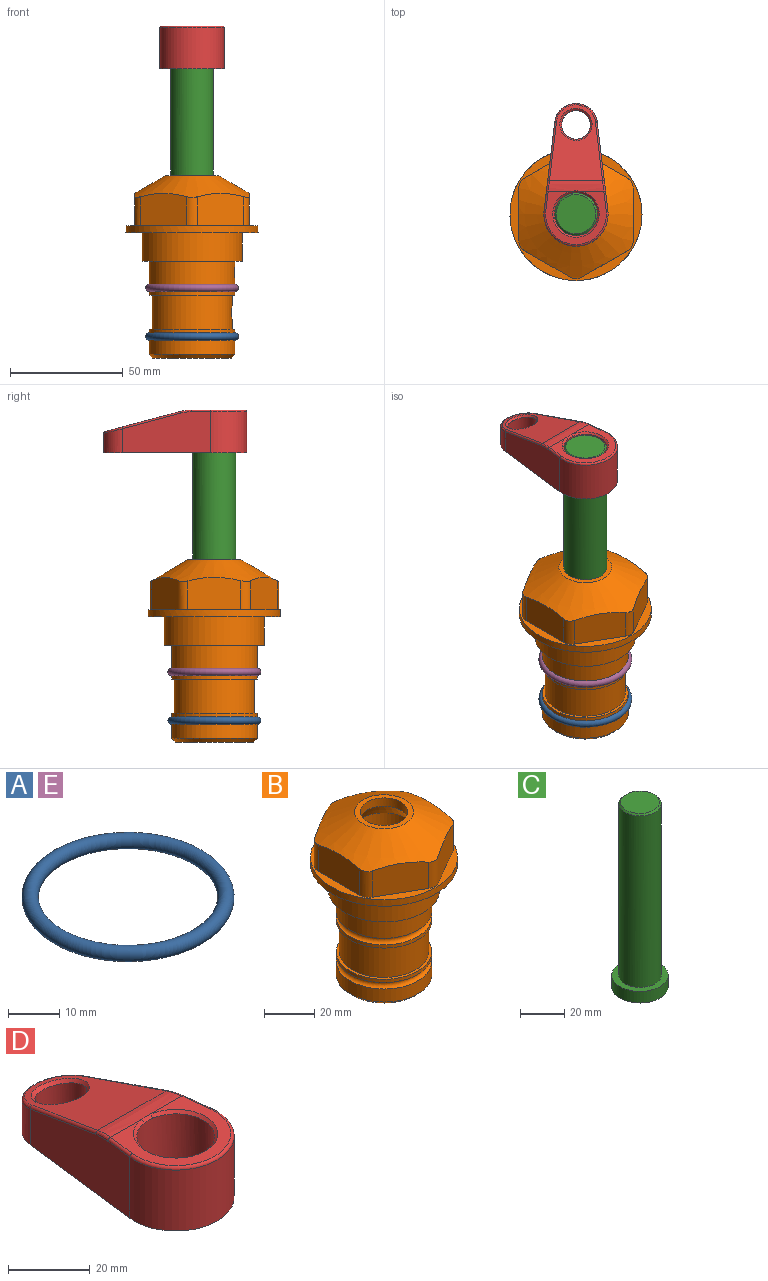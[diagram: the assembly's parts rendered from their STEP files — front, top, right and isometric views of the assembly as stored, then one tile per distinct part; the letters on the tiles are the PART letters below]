
ASSEMBLY  parts=5 mates=4
PART A: 1 faces, bbox 44.7x44.7x3.2 mm
  f0: torus R=19.05mm, axis (0,0,1), area 1193.9mm2
PART B: 36 faces, bbox 58.7x58.7x81 mm
  f0: cylinder r=17.78mm len=35.56mm, axis (0,0,1), area 1670.8mm2, adj f23,f24,f31
  f1: cylinder r=19.05mm len=38.1mm, axis (0,0,1), area 1191.9mm2, adj f26,f27,f30
  f2: plane 58.66x58.66mm, normal (0,0,-1), area 1150.6mm2, adj f3,f28
  f3: cylinder r=29.33mm len=58.66mm, axis (0,0,-1), area 585.1mm2, adj f2,f4
  f4: plane 58.66x58.66mm, normal (0,0,1), area 475.9mm2, adj f3,f5,f6,f7,f8,f9,f10,f11
  f5: plane 20.32x14.34mm, normal (-0.5,0.87,0), area 324.4mm2, adj f4,f15,f16,f17
  f6: plane 20.32x14.34mm, normal (0.5,0.87,0), area 324.4mm2, adj f4,f14,f15,f17
  f7: plane 23.48x14.34mm, normal (1,0,0), area 324.4mm2, adj f4,f13,f14,f17
  f8: plane 20.32x14.34mm, normal (0.5,-0.87,0), area 324.4mm2, adj f4,f12,f13,f17
  f9: plane 20.32x14.34mm, normal (-0.5,-0.87,0), area 324.4mm2, adj f4,f11,f12,f17
  f10: plane 23.48x14.34mm, normal (-1,0,0), area 324.4mm2, adj f4,f11,f16,f17
  f11: cylinder r=5.08mm len=12.85mm, axis (0,0,-1), area 67.2mm2, adj f4,f9,f10,f17
  f12: cylinder r=5.08mm len=12.85mm, axis (0,0,-1), area 67.2mm2, adj f4,f8,f9,f17
  f13: cylinder r=5.08mm len=12.85mm, axis (0,0,-1), area 67.2mm2, adj f4,f7,f8,f17
  f14: cylinder r=5.08mm len=12.85mm, axis (0,0,-1), area 67.2mm2, adj f4,f6,f7,f17
  f15: cylinder r=5.08mm len=12.85mm, axis (0,0,-1), area 67.2mm2, adj f4,f5,f6,f17
  f16: cylinder r=5.08mm len=12.85mm, axis (0,0,-1), area 67.2mm2, adj f4,f5,f10,f17
  f17: cone r=11.73mm half-angle=60deg, axis (0,0,-1), area 2071.8mm2, adj f5,f6,f7,f8,f9,f10,f11,f12
  f18: plane 23.46x23.46mm, normal (0,0,1), area 147.4mm2, adj f17,f35
  f19: plane 34.93x34.93mm, normal (0,0,-1), area 958mm2, adj f29
  f20: cylinder r=19.05mm len=38.1mm, axis (0,0,1), area 760.1mm2, adj f21,f29
  f21: torus R=19.05mm, axis (0,0,1), area 565.3mm2, adj f20,f22
  f22: cylinder r=19.05mm len=38.1mm, axis (0,0,1), area 190mm2, adj f21,f23
  f23: plane 38.1x38.1mm, normal (0,0,1), area 146.9mm2, adj f0,f22
  f24: plane 38.1x38.1mm, normal (0,0,-1), area 146.9mm2, adj f0,f25
  f25: cylinder r=19.05mm len=38.1mm, axis (0,0,1), area 190mm2, adj f24,f26
  f26: torus R=19.05mm, axis (0,0,1), area 565.3mm2, adj f1,f25
  f27: plane 44.45x44.45mm, normal (0,0,-1), area 411.7mm2, adj f1,f28
  f28: cylinder r=22.23mm len=44.45mm, axis (0,0,1), area 1773.5mm2, adj f2,f27
  f29: cone r=19.05mm half-angle=45deg, axis (0,0,1), area 257.5mm2, adj f19,f20
  f30: cylinder r=3.17mm len=6.75mm, axis (-1,0,0), area 128mm2, adj f1,f33
  f31: cylinder r=3.17mm len=6.35mm, axis (-1,0,0), area 102.5mm2, adj f0,f33
  f32: plane 25.4x25.4mm, normal (0,0,1), area 506.7mm2, adj f33
  f33: cylinder r=12.7mm len=66.42mm, axis (0,0,-1), area 5236.2mm2, adj f30,f31,f32,f34
  f34: cone r=9.53mm half-angle=30deg, axis (0,0,-1), area 443.4mm2, adj f33,f35
  f35: cylinder r=9.53mm len=19.05mm, axis (0,0,-1), area 240.9mm2, adj f18,f34
PART C: 6 faces, bbox 25.4x25.4x101.6 mm
  f0: plane 17.46x17.46mm, normal (0,0,1), area 239.5mm2, adj f5
  f1: plane 25.4x25.4mm, normal (0,0,-1), area 506.7mm2, adj f2
  f2: cylinder r=12.7mm len=25.4mm, axis (0,0,1), area 506.7mm2, adj f1,f3
  f3: plane 25.4x25.4mm, normal (0,0,1), area 221.7mm2, adj f2,f4
  f4: cylinder r=9.53mm len=94.46mm, axis (0,0,1), area 5653mm2, adj f3,f5
  f5: cone r=8.73mm half-angle=45deg, axis (0,0,-1), area 64.4mm2, adj f0,f4
PART D: 31 faces, bbox 31.7x65.5x19.8 mm
  f0: plane 39.12x18.26mm, normal (0.99,0.12,0), area 612.2mm2, adj f1,f4,f7,f11,f13,f15
  f1: cylinder r=9.53mm len=18.91mm, axis (0,0,-1), area 296.1mm2, adj f0,f2,f7,f17
  f2: plane 39.12x18.26mm, normal (-0.99,0.12,0), area 612.2mm2, adj f1,f4,f7,f12,f14,f16
  f3: cylinder r=6.35mm len=12.7mm, axis (0,0,-1), area 362.4mm2, adj f7,f18
  f4: cylinder r=14.29mm len=28.58mm, axis (0,0,-1), area 882.2mm2, adj f0,f2,f7,f10
  f5: cylinder r=9.53mm len=19.05mm, axis (0,0,-1), area 1092.6mm2, adj f7,f19,f20
  f6: plane 26.99x23.69mm, normal (0,0,1), area 216.2mm2, adj f9,f10,f11,f12,f19
  f7: plane 63.5x28.58mm, normal (0,0,-1), area 661.8mm2, adj f0,f1,f2,f3,f4,f5,f22,f23
  f8: plane 33.52x23.6mm, normal (0,0.26,0.97), area 486mm2, adj f9,f15,f16,f17,f18
  f9: cylinder r=19.05mm len=24.72mm, axis (1,0,0), area 120.4mm2, adj f6,f8,f13,f14,f20
  f10: torus R=13.49mm, axis (0,0,1), area 59mm2, adj f4,f6,f11,f12
  f11: cylinder r=0.79mm len=8.67mm, axis (0.12,-0.99,0), area 10.8mm2, adj f0,f6,f10,f13
  f12: cylinder r=0.79mm len=8.67mm, axis (0.12,0.99,0), area 10.8mm2, adj f2,f6,f10,f14
  f13: bspline ~4.95x1.42mm, area 6.1mm2, adj f0,f9,f11,f15
  f14: bspline ~4.95x1.42mm, area 6.1mm2, adj f2,f9,f12,f16
  f15: cylinder r=0.79mm len=25.95mm, axis (0.12,-0.96,0.26), area 32.9mm2, adj f0,f8,f13,f17
  f16: cylinder r=0.79mm len=25.95mm, axis (0.12,0.96,-0.26), area 32.9mm2, adj f2,f8,f14,f17
  f17: bspline ~18.91x8.38mm, area 30mm2, adj f1,f8,f15,f16
  f18: bspline ~14.29x14.29mm, area 48.3mm2, adj f3,f8
  f19: cone r=9.53mm half-angle=45deg, axis (0,0,1), area 66.5mm2, adj f5,f6,f20
  f20: bspline ~3.22x0.96mm, area 3.5mm2, adj f5,f9,f19
  f21: plane 2.75x2.72mm, normal (0,0,-1), area 2.9mm2, adj f23,f25,f28
  f22: plane 23.05x15.88mm, normal (-0.99,-0.12,0), area 323.6mm2, adj f7,f25,f26,f27,f28,f29
  f23: plane 23.05x15.88mm, normal (0.99,-0.12,0), area 323.6mm2, adj f7,f21,f25,f27,f28,f30
  f24: cylinder r=9.53mm len=10.69mm, axis (0,0,-1), area 114.7mm2, adj f7,f27,f29,f30
  f25: cylinder r=12.7mm len=20.59mm, axis (0,0,-1), area 381.1mm2, adj f7,f21,f22,f23,f26,f28
  f26: plane 2.75x2.72mm, normal (0,0,-1), area 2.9mm2, adj f22,f25,f28
  f27: plane 19.72x18.37mm, normal (0,-0.26,-0.97), area 291.8mm2, adj f22,f23,f24,f28,f29,f30
  f28: cylinder r=15.88mm len=19.92mm, axis (1,0,0), area 54.8mm2, adj f21,f22,f23,f25,f26,f27
  f29: cylinder r=1.59mm len=11mm, axis (0,0,-1), area 34.7mm2, adj f7,f22,f24,f27
  f30: cylinder r=1.59mm len=11mm, axis (0,0,-1), area 34.7mm2, adj f7,f23,f24,f27
PART E: same geometry as A
PLACE A t=(0,0,-21.59)mm
PLACE B at identity fixed
PLACE C t=(0,0,27.55)mm
PLACE D t=(0,0,28.35)mm
PLACE E at identity
MATE cylindrical B.f0 <-> C.f2  axis (0,0,1) through (0,0,-50.55)mm
MATE fastened D.f4 <-> C.f2  axis (0,0,-1) through (0,0,91.05)mm
MATE fastened B.f0 <-> A.f0  axis (0,0,1) through (0,0,-46.1)mm
MATE fastened B.f0 <-> E.f0  axis (0,0,1) through (0,0,-24.51)mm
